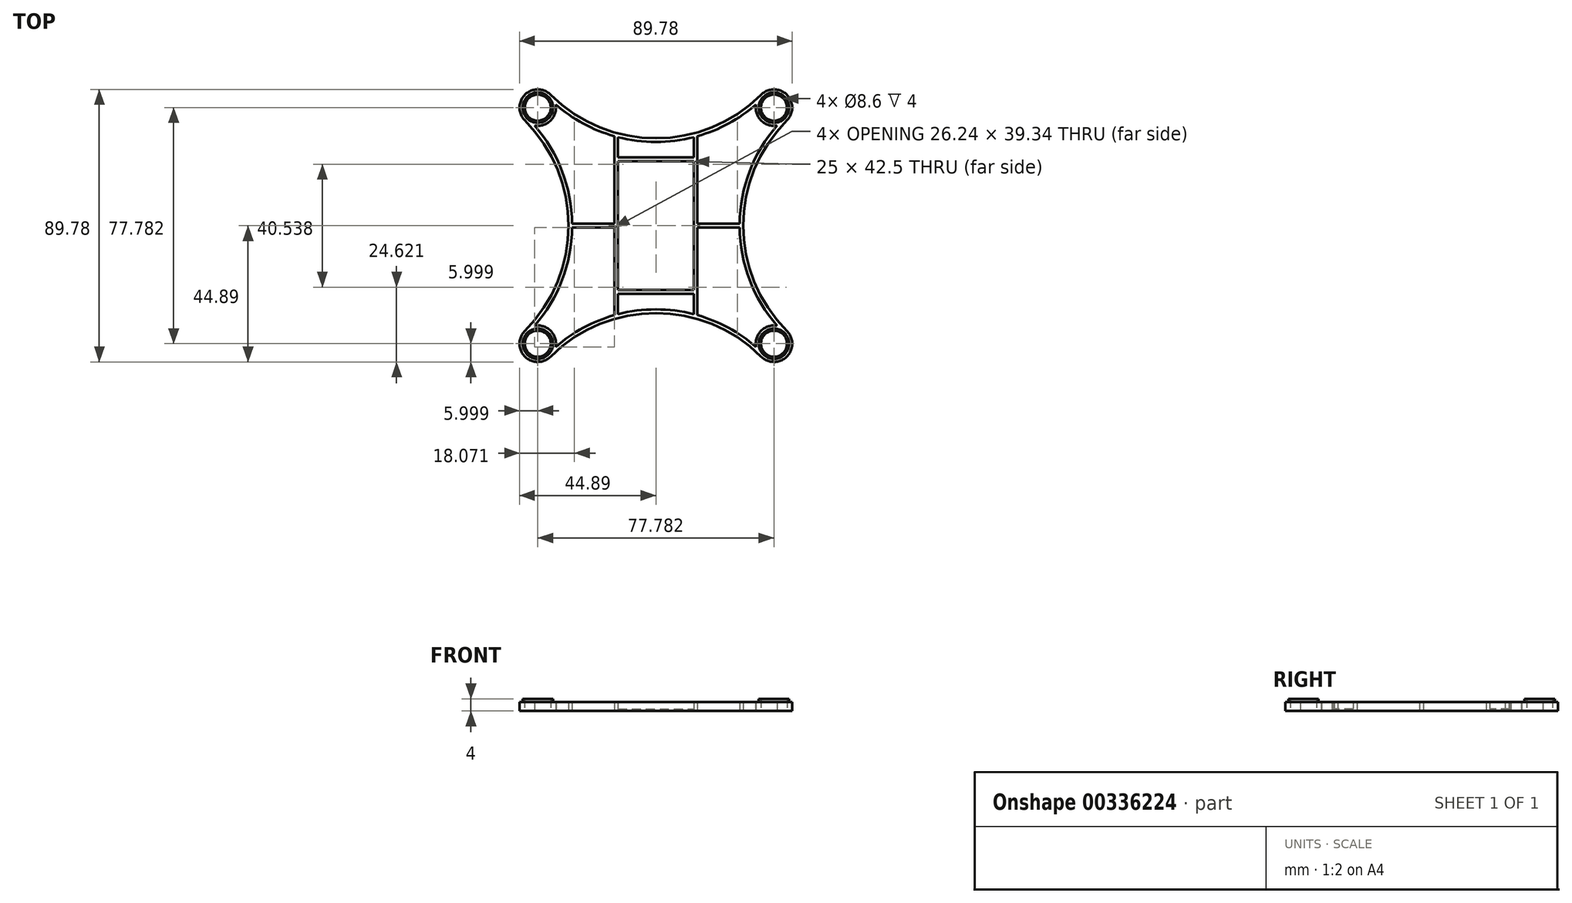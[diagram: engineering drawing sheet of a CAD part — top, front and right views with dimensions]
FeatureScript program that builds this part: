
annotation { "Feature Type Name" : "Feature", "Feature Type Description" : "" }
export const myFeature = defineFeature(function(context is Context, id is Id, definition is map)
    precondition{}
    {
        {
            var Q0;
            Q0=qCreatedBy(makeId("Top.planeOp"),FACE);
            var sketch = newSketch(context, id + "F0", { "sketchPlane" : qUnion([Q0])});
            skLineSegment(sketch, "E0.bottom", {"start": v(38.9, 38.9) * mm, "end": v(-38.9, 38.9) * mm, "construction": true});
            skLineSegment(sketch, "E0.top", {"start": v(38.9, -38.9) * mm, "end": v(-38.9, -38.9) * mm, "construction": true});
            skLineSegment(sketch, "E0.left", {"start": v(38.9, 38.9) * mm, "end": v(38.9, -38.9) * mm, "construction": true});
            skLineSegment(sketch, "E0.right", {"start": v(-38.9, 38.9) * mm, "end": v(-38.9, -38.9) * mm, "construction": true});
            skPoint(sketch, "E0.middle", {"position": v(0, 0) * mm});
            skCircle(sketch, "E1", {"center": v(38.9, 38.9) * mm, "radius": 4.25 * mm, "construction": true});
            skCircle(sketch, "E2", {"center": v(-38.9, 38.9) * mm, "radius": 4.25 * mm, "construction": true});
            skCircle(sketch, "E3", {"center": v(-38.9, -38.9) * mm, "radius": 4.25 * mm, "construction": true});
            skCircle(sketch, "E4", {"center": v(38.9, -38.9) * mm, "radius": 4.25 * mm, "construction": true});
            skLineSegment(sketch, "E5.bottom", {"start": v(10, 19.5) * mm, "end": v(-10, 19.5) * mm, "construction": true});
            skLineSegment(sketch, "E5.top", {"start": v(10, -13.5) * mm, "end": v(-10, -13.5) * mm, "construction": true});
            skLineSegment(sketch, "E5.left", {"start": v(10, 19.5) * mm, "end": v(10, -13.5) * mm, "construction": true});
            skLineSegment(sketch, "E5.right", {"start": v(-10, 19.5) * mm, "end": v(-10, -13.5) * mm, "construction": true});
            skLineSegment(sketch, "E6", {"start": v(38.9, 38.9) * mm, "end": v(-38.9, -38.9) * mm, "construction": true});
            skCircle(sketch, "E7", {"center": v(38.9, 38.9) * mm, "radius": 33 * mm, "construction": true});
            skCircle(sketch, "E8", {"center": v(-38.9, 38.9) * mm, "radius": 33 * mm, "construction": true});
            skCircle(sketch, "E9", {"center": v(-38.9, -38.9) * mm, "radius": 33 * mm, "construction": true});
            skCircle(sketch, "E10", {"center": v(38.9, -38.9) * mm, "radius": 33 * mm, "construction": true});
            skSolve(sketch);
        }
        {
            var Q0;
            Q0=qCreatedBy(makeId("Top.planeOp"),FACE);
            var sketch = newSketch(context, id + "F1", { "sketchPlane" : qUnion([Q0])});
            skCircle(sketch, "E11.0", {"center": v(-38.9, 38.9) * mm, "radius": 4.25 * mm, "construction": true});
            skCircle(sketch, "E12.0", {"center": v(38.9, 38.9) * mm, "radius": 4.25 * mm, "construction": true});
            skCircle(sketch, "E13.0", {"center": v(-38.9, -38.9) * mm, "radius": 4.25 * mm, "construction": true});
            skCircle(sketch, "E14.0", {"center": v(38.9, -38.9) * mm, "radius": 4.25 * mm, "construction": true});
            skCircle(sketch, "E15", {"center": v(-38.9, 38.9) * mm, "radius": 6 * mm, "construction": true});
            skCircle(sketch, "E16.1.0", {"center": v(-38.9, -38.9) * mm, "radius": 6 * mm, "construction": true});
            skCircle(sketch, "E16.2.0", {"center": v(38.9, -38.9) * mm, "radius": 6 * mm, "construction": true});
            skCircle(sketch, "E16.3.0", {"center": v(38.9, 38.9) * mm, "radius": 6 * mm, "construction": true});
            skPoint(sketch, "E16.center", {"position": v(0, 0) * mm});
            skArc(sketch, "E17", {"start": v(-43.13, 34.65) * mm, "mid": v(-28.78, 0) * mm, "end": v(-43.13, -34.65) * mm});
            skLineSegment(sketch, "E18", {"start": v(-43.13, -34.65) * mm, "end": v(-38.9, -38.9) * mm, "construction": true});
            skArc(sketch, "E19.1.0", {"start": v(-34.65, -43.13) * mm, "mid": v(0, -28.78) * mm, "end": v(34.65, -43.13) * mm});
            skArc(sketch, "E19.2.0", {"start": v(43.13, -34.65) * mm, "mid": v(28.78, 0) * mm, "end": v(43.13, 34.65) * mm});
            skArc(sketch, "E19.3.0", {"start": v(34.65, 43.13) * mm, "mid": v(0, 28.78) * mm, "end": v(-34.65, 43.13) * mm});
            skArc(sketch, "E20", {"start": v(-43.13, 34.65) * mm, "mid": v(-43.13, 43.13) * mm, "end": v(-34.65, 43.13) * mm});
            skArc(sketch, "E21", {"start": v(34.65, 43.13) * mm, "mid": v(43.13, 43.13) * mm, "end": v(43.13, 34.65) * mm});
            skArc(sketch, "E22", {"start": v(-43.13, -34.65) * mm, "mid": v(-43.13, -43.13) * mm, "end": v(-34.65, -43.13) * mm});
            skArc(sketch, "E23", {"start": v(34.65, -43.13) * mm, "mid": v(43.13, -43.13) * mm, "end": v(43.13, -34.65) * mm});
            skArc(sketch, "E24.1", {"start": v(35.5, 42.28) * mm, "mid": v(0, 27.58) * mm, "end": v(-35.5, 42.28) * mm});
            skArc(sketch, "E24.2", {"start": v(-42.28, 35.5) * mm, "mid": v(-27.58, 0) * mm, "end": v(-42.28, -35.5) * mm});
            skArc(sketch, "E24.5", {"start": v(-35.5, -42.28) * mm, "mid": v(0, -27.58) * mm, "end": v(35.5, -42.28) * mm});
            skArc(sketch, "E24.7", {"start": v(42.28, -35.5) * mm, "mid": v(27.58, 0) * mm, "end": v(42.28, 35.5) * mm});
            skArc(sketch, "E25", {"start": v(-32.98, 39.94) * mm, "mid": v(-34.65, 34.65) * mm, "end": v(-39.94, 32.98) * mm});
            skArc(sketch, "E26.1.0", {"start": v(-39.94, -32.98) * mm, "mid": v(-34.65, -34.65) * mm, "end": v(-32.98, -39.94) * mm});
            skArc(sketch, "E26.2.0", {"start": v(32.98, -39.94) * mm, "mid": v(34.65, -34.65) * mm, "end": v(39.94, -32.98) * mm});
            skArc(sketch, "E26.3.0", {"start": v(39.94, 32.98) * mm, "mid": v(34.65, 34.65) * mm, "end": v(32.98, 39.94) * mm});
            skLineSegment(sketch, "E27", {"start": v(-38.9, 38.9) * mm, "end": v(38.9, -38.9) * mm, "construction": true});
            skLineSegment(sketch, "E28.0", {"start": v(38.9, 38.9) * mm, "end": v(-38.9, -38.9) * mm, "construction": true});
            skSolve(sketch);
        }
        {
            var Q0;
            Q0=qCreatedBy(makeId("Top.planeOp"),FACE);
            var sketch = newSketch(context, id + "F2", { "sketchPlane" : qUnion([Q0])});
            skArc(sketch, "E29.0", {"start": v(35.5, 42.28) * mm, "mid": v(25.42, 34.5) * mm, "end": v(13.7, 29.49) * mm, "construction": true});
            skArc(sketch, "E30.0", {"start": v(-35.5, -42.28) * mm, "mid": v(-25.42, -34.5) * mm, "end": v(-13.7, -29.49) * mm, "construction": true});
            skLineSegment(sketch, "E31", {"start": v(-12.5, 29.16) * mm, "end": v(-12.5, -29.16) * mm});
            skLineSegment(sketch, "E32", {"start": v(-13.7, 29.49) * mm, "end": v(-13.7, -29.49) * mm});
            skLineSegment(sketch, "E33.MirrorCS", {"start": v(12.5, 29.16) * mm, "end": v(12.5, -29.16) * mm});
            skLineSegment(sketch, "E34.MirrorCS", {"start": v(13.7, 29.49) * mm, "end": v(13.7, -29.49) * mm});
            skLineSegment(sketch, "E35", {"start": v(-12.5, 22.45) * mm, "end": v(12.5, 22.45) * mm});
            skLineSegment(sketch, "E36.MirrorCS", {"start": v(-12.5, -22.45) * mm, "end": v(12.5, -22.45) * mm});
            skArc(sketch, "E37", {"start": v(-13.7, 29.49) * mm, "mid": v(-25.42, 34.5) * mm, "end": v(-35.5, 42.28) * mm, "construction": true});
            skArc(sketch, "E38", {"start": v(-12.5, 29.16) * mm, "mid": v(-13.1, 29.32) * mm, "end": v(-13.7, 29.49) * mm});
            skArc(sketch, "E39", {"start": v(12.5, 29.16) * mm, "mid": v(0, 27.58) * mm, "end": v(-12.5, 29.16) * mm});
            skArc(sketch, "E40", {"start": v(13.7, 29.49) * mm, "mid": v(13.1, 29.32) * mm, "end": v(12.5, 29.16) * mm});
            skArc(sketch, "E41", {"start": v(-13.7, -29.49) * mm, "mid": v(-13.1, -29.32) * mm, "end": v(-12.5, -29.16) * mm});
            skArc(sketch, "E42", {"start": v(-12.5, -29.16) * mm, "mid": v(0, -27.58) * mm, "end": v(12.5, -29.16) * mm});
            skArc(sketch, "E43", {"start": v(12.5, -29.16) * mm, "mid": v(13.1, -29.32) * mm, "end": v(13.7, -29.49) * mm});
            skArc(sketch, "E44", {"start": v(13.7, -29.49) * mm, "mid": v(25.42, -34.5) * mm, "end": v(35.5, -42.28) * mm, "construction": true});
            skLineSegment(sketch, "E45", {"start": v(-12.5, 21.25) * mm, "end": v(12.5, 21.25) * mm});
            skLineSegment(sketch, "E46.MirrorCS", {"start": v(-12.5, -21.25) * mm, "end": v(12.5, -21.25) * mm});
            skLineSegment(sketch, "E47", {"start": v(-13.7, 23.25) * mm, "end": v(-15.7, 23.25) * mm});
            skLineSegment(sketch, "E48", {"start": v(-15.7, 21.25) * mm, "end": v(-13.7, 21.25) * mm});
            skLineSegment(sketch, "E49.MirrorCS", {"start": v(13.7, 23.25) * mm, "end": v(15.7, 23.25) * mm});
            skLineSegment(sketch, "E50.MirrorCS", {"start": v(15.7, 21.25) * mm, "end": v(13.7, 21.25) * mm});
            skLineSegment(sketch, "E51.MirrorCS", {"start": v(-13.7, -23.25) * mm, "end": v(-15.7, -23.25) * mm});
            skLineSegment(sketch, "E52.MirrorCS", {"start": v(-15.7, -21.25) * mm, "end": v(-13.7, -21.25) * mm});
            skLineSegment(sketch, "E53.MirrorCS", {"start": v(13.7, -23.25) * mm, "end": v(15.7, -23.25) * mm});
            skLineSegment(sketch, "E54.MirrorCS", {"start": v(15.7, -21.25) * mm, "end": v(13.7, -21.25) * mm});
            skLineSegment(sketch, "E55", {"start": v(-15.7, 23.25) * mm, "end": v(-15.7, 21.25) * mm});
            skLineSegment(sketch, "E56", {"start": v(15.7, 23.25) * mm, "end": v(15.7, 21.25) * mm});
            skLineSegment(sketch, "E57", {"start": v(-15.7, -21.25) * mm, "end": v(-15.7, -23.25) * mm});
            skLineSegment(sketch, "E58", {"start": v(15.7, -21.25) * mm, "end": v(15.7, -23.25) * mm});
            skArc(sketch, "E59.0", {"start": v(-42.28, 35.5) * mm, "mid": v(-31.52, 19.49) * mm, "end": v(-27.59, 0.6) * mm, "construction": true});
            skArc(sketch, "E60.0", {"start": v(42.28, -35.5) * mm, "mid": v(27.58, 0) * mm, "end": v(42.28, 35.5) * mm, "construction": true});
            skLineSegment(sketch, "E61", {"start": v(-27.59, 0.6) * mm, "end": v(-13.7, 0.6) * mm});
            skLineSegment(sketch, "E62", {"start": v(-27.59, -0.6) * mm, "end": v(-13.7, -0.6) * mm});
            skArc(sketch, "E63", {"start": v(-27.59, 0.6) * mm, "mid": v(-27.58, 0) * mm, "end": v(-27.59, -0.6) * mm});
            skArc(sketch, "E64", {"start": v(-27.59, -0.6) * mm, "mid": v(-31.52, -19.49) * mm, "end": v(-42.28, -35.5) * mm, "construction": true});
            skLineSegment(sketch, "E65", {"start": v(0, 0) * mm, "end": v(0, 58.8) * mm, "construction": true});
            skLineSegment(sketch, "E66.MirrorCS", {"start": v(27.59, -0.6) * mm, "end": v(13.7, -0.6) * mm});
            skLineSegment(sketch, "E67.MirrorCS", {"start": v(27.59, 0.6) * mm, "end": v(13.7, 0.6) * mm});
            skArc(sketch, "E68.MirrorCS", {"start": v(27.59, 0.6) * mm, "mid": v(27.58, 0) * mm, "end": v(27.59, -0.6) * mm});
            skSolve(sketch);
        }
        {
            var Q0;
            Q0=qCreatedBy(makeId("Top.planeOp"),FACE);
            var sketch = newSketch(context, id + "F3", { "sketchPlane" : qUnion([Q0])});
            skCircle(sketch, "E69.0", {"center": v(-38.9, 38.9) * mm, "radius": 4.25 * mm, "construction": true});
            skCircle(sketch, "E70.0", {"center": v(38.9, 38.9) * mm, "radius": 4.25 * mm, "construction": true});
            skCircle(sketch, "E71.0", {"center": v(-38.9, -38.9) * mm, "radius": 4.25 * mm, "construction": true});
            skCircle(sketch, "E72.0", {"center": v(38.9, -38.9) * mm, "radius": 4.25 * mm, "construction": true});
            skCircle(sketch, "E73", {"center": v(-38.9, 38.9) * mm, "radius": 5 * mm});
            skCircle(sketch, "E74", {"center": v(38.9, 38.9) * mm, "radius": 5 * mm});
            skCircle(sketch, "E75", {"center": v(-38.9, -38.9) * mm, "radius": 5 * mm});
            skCircle(sketch, "E76", {"center": v(38.9, -38.9) * mm, "radius": 5 * mm});
            skSolve(sketch);
        }
        {
            var Q0;
            Q0 = qSketchRegion(id + "F1", true);
            extrude(context, id + "F4", {"entities" : qUnion([Q0]), "depth" : 3 * mm});
        }
        {
            var Q0;
            Q0 = qSketchRegion(id + "F3", true);
            extrude(context, id + "F5", {"entities" : qUnion([Q0]), "operationType" : NewBodyOperationType.ADD, "depth" : 4 * mm});
        }
        {
            var Q0;
            Q0=qCreatedBy(makeId("Top.planeOp"),FACE);
            var sketch = newSketch(context, id + "F6", { "sketchPlane" : qUnion([Q0])});
            skPoint(sketch, "E77.0", {"position": v(-38.9, 38.9) * mm});
            skPoint(sketch, "E78.0", {"position": v(38.9, 38.9) * mm});
            skPoint(sketch, "E79.0", {"position": v(-38.9, -38.9) * mm});
            skPoint(sketch, "E80.0", {"position": v(38.9, -38.9) * mm});
            skCircle(sketch, "E81", {"center": v(-38.9, 38.9) * mm, "radius": 4.3 * mm});
            skCircle(sketch, "E82", {"center": v(38.9, 38.9) * mm, "radius": 4.3 * mm});
            skCircle(sketch, "E83", {"center": v(-38.9, -38.9) * mm, "radius": 4.3 * mm});
            skCircle(sketch, "E84", {"center": v(38.9, -38.9) * mm, "radius": 4.3 * mm});
            skSolve(sketch);
        }
        {
            var Q0;
            Q0=makeQuery(id+"F2.imprint","IMPRINT",FACE,{"disambiguationData":[TD([[makeQuery(id+"F2.imprint","IMPRINT",EDGE,{"derivedFrom":sQuery(id+"F2.wireOp",EDGE,"E32")}),1.0]])]});
            var Q1;
            Q1=makeQuery(id+"F2.imprint","IMPRINT",FACE,{"disambiguationData":[TD([[makeQuery(id+"F2.imprint","IMPRINT",EDGE,{"derivedFrom":sQuery(id+"F2.wireOp",EDGE,"E34.MirrorCS")}),-1.0]])]});
            var Q2;
            {var subQ0=sQuery(id+"F2.wireOp",EDGE,"E35");Q2=makeQuery(id+"F2.imprint","IMPRINT",FACE,{"disambiguationData":[TD([[makeQuery(id+"F2.imprint","IMPRINT",EDGE,{"derivedFrom":subQ0}),-1.0]])]});}
            var Q3;
            {var subQ0=sQuery(id+"F2.wireOp",EDGE,"E36.MirrorCS");Q3=makeQuery(id+"F2.imprint","IMPRINT",FACE,{"disambiguationData":[TD([[makeQuery(id+"F2.imprint","IMPRINT",EDGE,{"derivedFrom":subQ0}),1.0]])]});}
            var Q4;
            {var subQ0=sQuery(id+"F2.wireOp",EDGE,"E61");Q4=makeQuery(id+"F2.imprint","IMPRINT",FACE,{"disambiguationData":[TD([[makeQuery(id+"F2.imprint","IMPRINT",EDGE,{"derivedFrom":subQ0}),-1.0]])]});}
            var Q5;
            {var subQ0=sQuery(id+"F2.wireOp",EDGE,"E66.MirrorCS");Q5=makeQuery(id+"F2.imprint","IMPRINT",FACE,{"disambiguationData":[TD([[makeQuery(id+"F2.imprint","IMPRINT",EDGE,{"derivedFrom":subQ0}),-1.0]])]});}
            var Q6;
            Q6=makeQuery(id+"F4.opExtrude","CAP_FACE",FACE,{"disambiguationData":[OSD([sQuery(id+"F1.wireOp",EDGE,"E17"),sQuery(id+"F1.wireOp",EDGE,"E19.1.0"),sQuery(id+"F1.wireOp",EDGE,"E19.2.0"),sQuery(id+"F1.wireOp",EDGE,"E19.3.0"),sQuery(id+"F1.wireOp",EDGE,"E20"),sQuery(id+"F1.wireOp",EDGE,"E21"),sQuery(id+"F1.wireOp",EDGE,"E22"),sQuery(id+"F1.wireOp",EDGE,"E23"),sQuery(id+"F1.wireOp",EDGE,"E24.1"),sQuery(id+"F1.wireOp",EDGE,"E24.2"),sQuery(id+"F1.wireOp",EDGE,"E24.5"),sQuery(id+"F1.wireOp",EDGE,"E24.7"),sQuery(id+"F1.wireOp",EDGE,"E25"),sQuery(id+"F1.wireOp",EDGE,"E26.1.0"),sQuery(id+"F1.wireOp",EDGE,"E26.2.0"),sQuery(id+"F1.wireOp",EDGE,"E26.3.0")])],"isStart":false});
            extrude(context, id + "F7", {"entities" : qUnion([Q0, Q1, Q2, Q3, Q4, Q5]), "operationType" : NewBodyOperationType.ADD, "endBound" : BoundingType.UP_TO_SURFACE, "endBoundEntityFace" : qUnion([Q6]), "depth" : 25 * mm});
        }
        {
            var Q0;
            {var subQ2=sQuery(id+"F2.wireOp",EDGE,"E35");Q0=makeQuery(id+"F2.imprint","IMPRINT",FACE,{"disambiguationData":[TD([[makeQuery(id+"F2.imprint","IMPRINT",EDGE,{"derivedFrom":subQ2}),1.0]])]});}
            var Q1;
            {var subQ2=sQuery(id+"F2.wireOp",EDGE,"E36.MirrorCS");Q1=makeQuery(id+"F2.imprint","IMPRINT",FACE,{"disambiguationData":[TD([[makeQuery(id+"F2.imprint","IMPRINT",EDGE,{"derivedFrom":subQ2}),-1.0]])]});}
            extrude(context, id + "F8", {"entities" : qUnion([Q0, Q1]), "operationType" : NewBodyOperationType.ADD, "depth" : (0.2 * 3) * mm});
        }
        {
            var Q0;
            Q0 = qSketchRegion(id + "F6", true);
            extrude(context, id + "F9", {"entities" : qUnion([Q0]), "operationType" : NewBodyOperationType.REMOVE, "endBound" : BoundingType.THROUGH_ALL, "depth" : 25 * mm});
        }
    });
